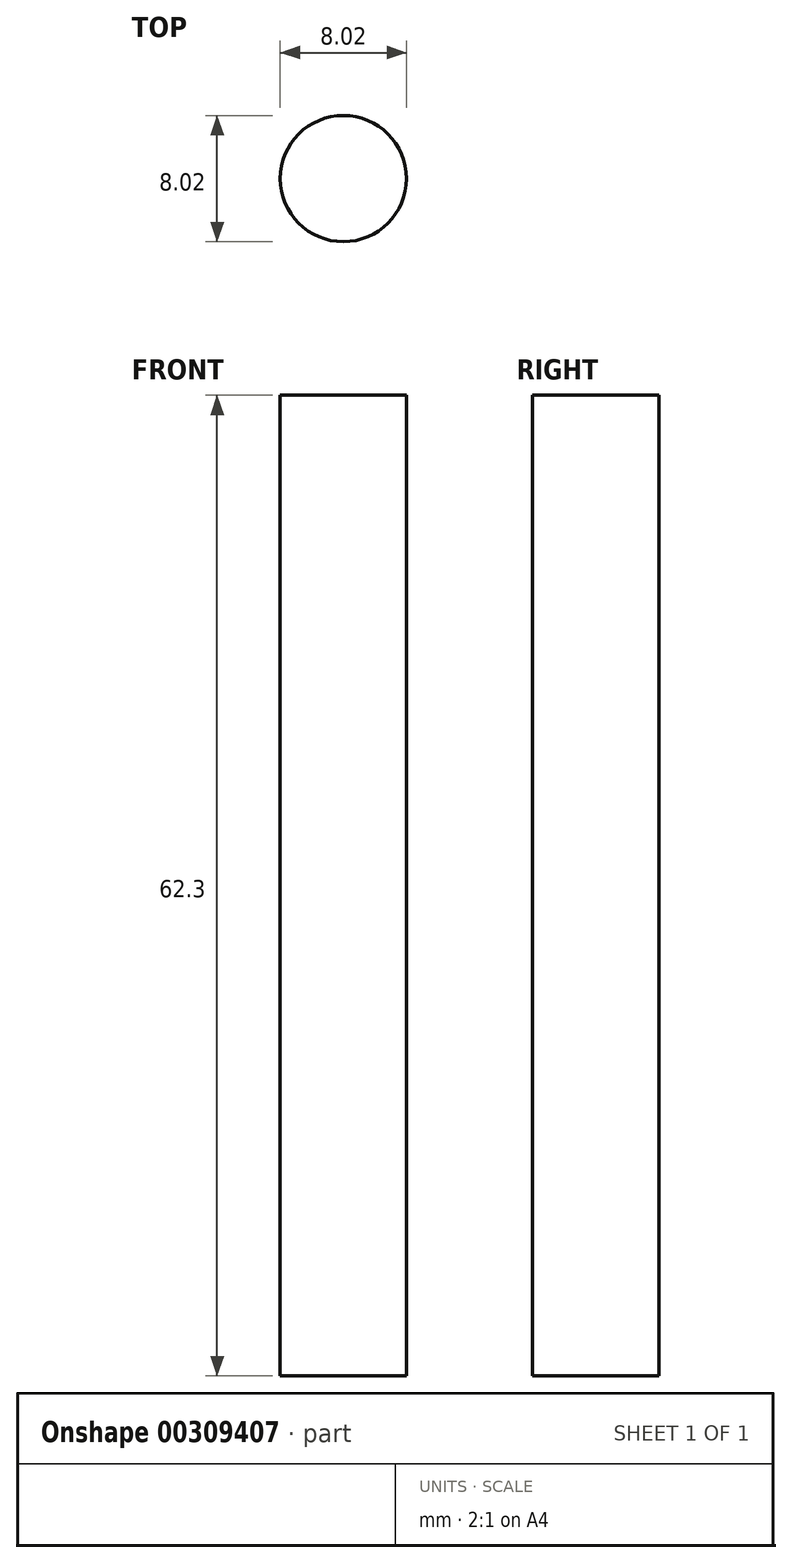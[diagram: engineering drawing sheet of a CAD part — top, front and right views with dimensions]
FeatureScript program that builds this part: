
annotation { "Feature Type Name" : "Feature", "Feature Type Description" : "" }
export const myFeature = defineFeature(function(context is Context, id is Id, definition is map)
    precondition{}
    {
        {
            var Q0;
            Q0=qCreatedBy(makeId("Top.planeOp"),FACE);
            var sketch = newSketch(context, id + "F0", { "sketchPlane" : qUnion([Q0])});
            skCircle(sketch, "E0", {"center": v(0, 0) * mm, "radius": 4 * mm});
            skSolve(sketch);
        }
        {
            var Q0;
            Q0=makeQuery(id+"F0.imprint","IMPRINT",FACE,{"disambiguationData":[TD([[makeQuery(id+"F0.imprint","IMPRINT",EDGE,{"derivedFrom":sQuery(id+"F0.wireOp",EDGE,"E0")}),1.0]])]});
            extrude(context, id + "F1", {"entities" : qUnion([Q0]), "depth" : 62.3 * mm});
        }
    });
